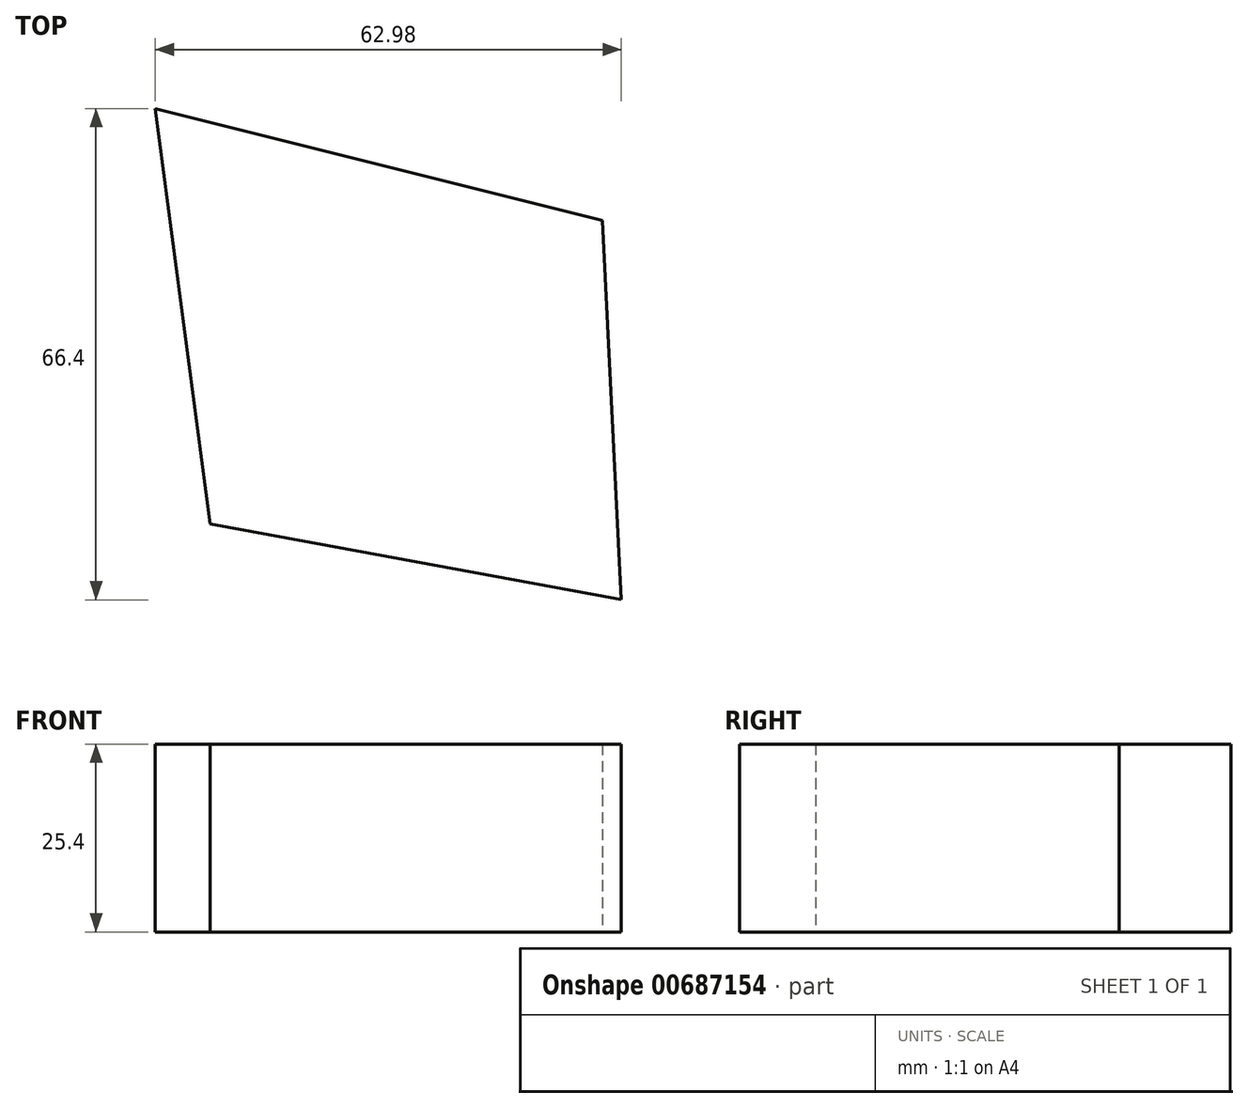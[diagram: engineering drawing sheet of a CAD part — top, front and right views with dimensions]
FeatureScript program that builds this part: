
annotation { "Feature Type Name" : "Feature", "Feature Type Description" : "" }
export const myFeature = defineFeature(function(context is Context, id is Id, definition is map)
    precondition{}
    {
        {
            var Q0;
            Q0=qCreatedBy(makeId("Top.planeOp"),FACE);
            var sketch = newSketch(context, id + "F0", { "sketchPlane" : qUnion([Q0])});
            skLineSegment(sketch, "E0", {"start": v(-61.08, -34.45) * mm, "end": v(-68.48, 21.68) * mm});
            skLineSegment(sketch, "E1", {"start": v(-68.48, 21.68) * mm, "end": v(-8.04, 6.58) * mm});
            skLineSegment(sketch, "E2", {"start": v(-8.04, 6.58) * mm, "end": v(-5.5, -44.72) * mm});
            skLineSegment(sketch, "E3", {"start": v(-5.5, -44.72) * mm, "end": v(-61.08, -34.45) * mm});
            skSolve(sketch);
        }
        {
            var Q0;
            Q0 = qSketchRegion(id + "F0", true);
            extrude(context, id + "F1", {"entities" : qUnion([Q0]), "depth" : 25.4 * mm, "offsetDistance" : 25.4 * mm});
        }
    });
